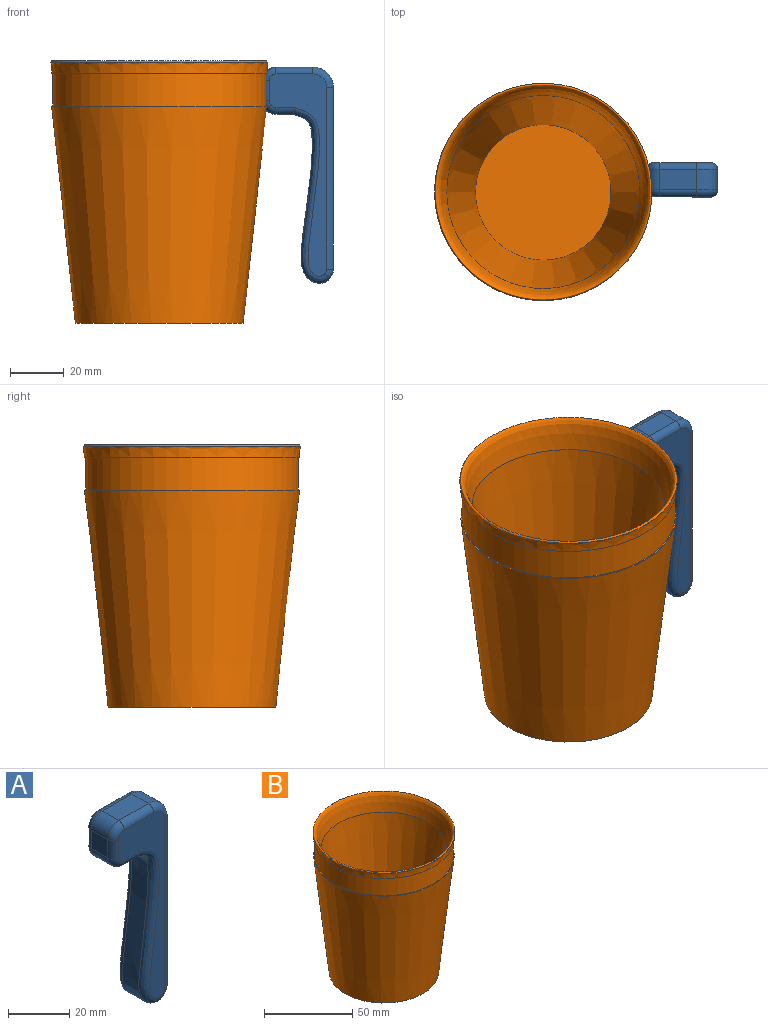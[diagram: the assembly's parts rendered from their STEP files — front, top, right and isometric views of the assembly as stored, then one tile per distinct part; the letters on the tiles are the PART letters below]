
ASSEMBLY  parts=2 mates=1
PART A: 29 faces, bbox 27.4x12.7x80.7 mm
  f0: plane 75.03x21.29mm, normal (0,-1,0), area 551.8mm2, adj f10,f11,f12,f13,f14,f15,f16,f17
  f1: plane 75.03x21.29mm, normal (0,1,0), area 551.9mm2, adj f18,f19,f20,f21,f22,f23,f24,f25
  f2: plane 7.62x7.41mm, normal (-1,0,0), area 56.5mm2, adj f7,f8,f12,f19
  f3: plane 7.62x6.5mm, normal (0,0,-1), area 49.5mm2, adj f4,f7,f11,f20
  f4: extruded ~62.54x13.44mm, area 567.4mm2, adj f3,f13,f22,f27
  f5: plane 67.22x7.62mm, normal (1,0,0), area 512.2mm2, adj f9,f15,f24,f27
  f6: plane 13.67x7.62mm, normal (0,0,1), area 104.2mm2, adj f8,f9,f16,f23
  f7: cylinder r=5.08mm len=7.62mm, axis (0,-1,0), area 60.8mm2, adj f2,f3,f10,f18
  f8: cylinder r=5.08mm len=7.62mm, axis (0,-1,0), area 60.8mm2, adj f2,f6,f14,f21
  f9: cylinder r=7.62mm len=7.62mm, axis (0,-1,0), area 91.2mm2, adj f5,f6,f17,f25
  f10: torus R=2.54mm, axis (0,-1,0), area 26.1mm2, adj f0,f7,f11,f12
  f11: cylinder r=2.54mm len=6.85mm, axis (-1,0,0), area 26.6mm2, adj f0,f3,f10,f13
  f12: cylinder r=2.54mm len=7.41mm, axis (0,0,1), area 29.6mm2, adj f0,f2,f10,f14
  f13: bspline ~65.31x14.82mm, area 293.8mm2, adj f0,f4,f11,f26
  f14: torus R=2.54mm, axis (0,-1,0), area 26.1mm2, adj f0,f8,f12,f16
  f15: cylinder r=2.54mm len=67.22mm, axis (0,0,-1), area 268.2mm2, adj f0,f5,f17,f26
  f16: cylinder r=2.54mm len=13.67mm, axis (1,0,0), area 54.6mm2, adj f0,f6,f14,f17
  f17: torus R=5.08mm, axis (0,-1,0), area 42mm2, adj f0,f9,f15,f16
  f18: torus R=2.54mm, axis (0,-1,0), area 26.1mm2, adj f1,f7,f19,f20
  f19: cylinder r=2.54mm len=7.41mm, axis (0,0,-1), area 29.6mm2, adj f1,f2,f18,f21
  f20: cylinder r=2.54mm len=6.85mm, axis (1,0,0), area 26.6mm2, adj f1,f3,f18,f22
  f21: torus R=2.54mm, axis (0,-1,0), area 26.1mm2, adj f1,f8,f19,f23
  f22: bspline ~65.31x14.82mm, area 293.8mm2, adj f1,f4,f20,f28
  f23: cylinder r=2.54mm len=13.67mm, axis (-1,0,0), area 54.6mm2, adj f1,f6,f21,f25
  f24: cylinder r=2.54mm len=67.22mm, axis (0,0,1), area 268.2mm2, adj f1,f5,f25,f28
  f25: torus R=5.08mm, axis (0,-1,0), area 42mm2, adj f1,f9,f23,f24
  f26: torus R=2.54mm, axis (0,-1,0), area 12.4mm2, adj f0,f13,f15,f27
  f27: cylinder r=5.08mm len=7.62mm, axis (0,1,0), area 28.9mm2, adj f4,f5,f26,f28
  f28: torus R=2.54mm, axis (0,-1,0), area 12.4mm2, adj f1,f22,f24,f27
PART B: 9 faces, bbox 80.6x80.6x97.2 mm
  f0: plane 50.23x50.23mm, normal (0,0,1), area 1981.7mm2, adj f8
  f1: plane 62.2x62.2mm, normal (0,0,-1), area 3038.4mm2, adj f2
  f2: cone r=31.1mm half-angle=6.2deg, axis (0,0,1), area 18045.3mm2, adj f1,f3
  f3: plane 79.76x79.76mm, normal (0,0,1), area 111.2mm2, adj f2,f4
  f4: cylinder r=39.44mm len=78.87mm, axis (0,0,-1), area 3028.3mm2, adj f3,f5
  f5: plane 79.76x79.76mm, normal (0,0,-1), area 111.2mm2, adj f4,f6
  f6: revolved ~80.58x80.58mm, area 1025.7mm2, adj f5,f7
  f7: revolved ~80.58x80.58mm, area 3169.5mm2, adj f6,f8
  f8: cone r=25.12mm half-angle=7.5deg, axis (0,0,1), area 15684.9mm2, adj f0,f7
PLACE A t=(71.9,-26.24,74.81)mm
PLACE B t=(33.75,-37.16,1.63)mm
MATE parallel B.f2 <-> A.f3  axis (0,0,-1) through (33.75,-37.16,-2.5)mm
